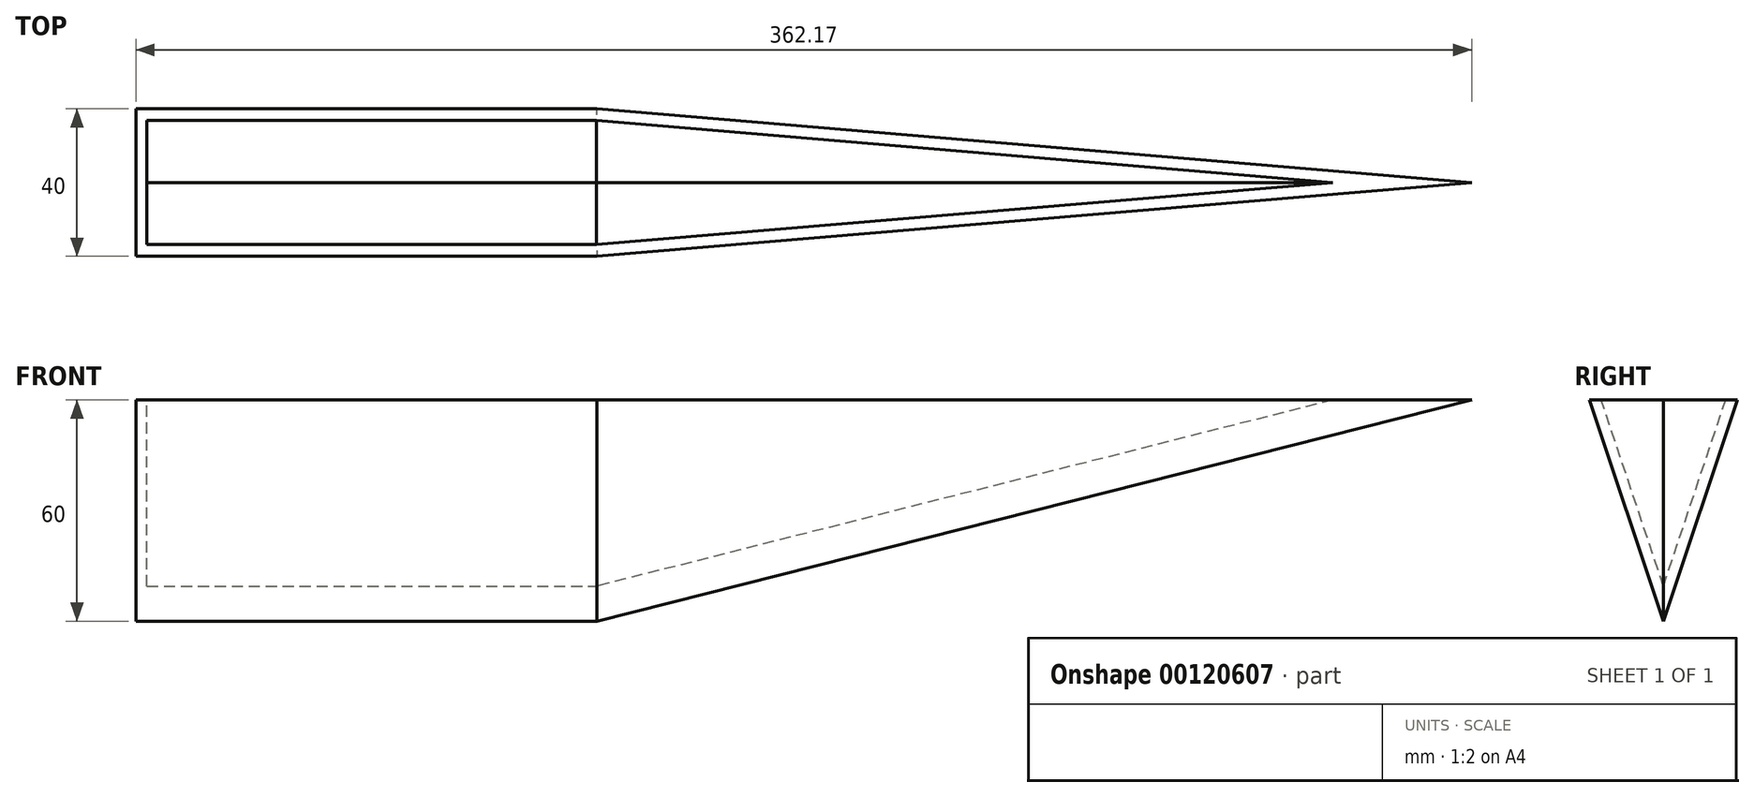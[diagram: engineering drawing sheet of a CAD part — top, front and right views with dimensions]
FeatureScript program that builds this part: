
annotation { "Feature Type Name" : "Feature", "Feature Type Description" : "" }
export const myFeature = defineFeature(function(context is Context, id is Id, definition is map)
    precondition{}
    {
        {
            var Q0;
            Q0=qCreatedBy(makeId("Front.planeOp"),FACE);
            var sketch = newSketch(context, id + "F0", { "sketchPlane" : qUnion([Q0])});
            skLineSegment(sketch, "E0.bottom", {"start": v(-391.71, 45.8) * mm, "end": v(-16.71, 45.8) * mm});
            skLineSegment(sketch, "E0.top", {"start": v(-391.71, -14.2) * mm, "end": v(-16.71, -14.2) * mm});
            skLineSegment(sketch, "E0.left", {"start": v(-391.71, 45.8) * mm, "end": v(-391.71, -14.2) * mm});
            skLineSegment(sketch, "E0.right", {"start": v(-16.71, 45.8) * mm, "end": v(-16.71, -14.2) * mm});
            skPoint(sketch, "E1.endSnap0", {"position": v(-204.21, -14.2) * mm});
            skSolve(sketch);
        }
        {
            var Q0;
            Q0=makeQuery(id+"F0.imprint","IMPRINT",FACE,{"disambiguationData":[TD([[makeQuery(id+"F0.imprint","IMPRINT",EDGE,{"derivedFrom":sQuery(id+"F0.wireOp",EDGE,"E0.bottom")}),-1.0]])]});
            extrude(context, id + "F1", {"entities" : qUnion([Q0]), "depth" : 40 * mm});
        }
        {
            var Q0;
            Q0=makeQuery(id+"F1.opExtrude","SWEPT_FACE",FACE,{"disambiguationData":[OSD([sQuery(id+"F0.wireOp",EDGE,"E0.left")])]});
            var sketch = newSketch(context, id + "F2", { "sketchPlane" : qUnion([Q0])});
            skLineSegment(sketch, "E2", {"start": v(20, -14.2) * mm, "end": v(0, 45.8) * mm});
            skLineSegment(sketch, "E3", {"start": v(20, -14.2) * mm, "end": v(40, 45.8) * mm});
            skSolve(sketch);
        }
        {
            var Q0;
            {var subQ0=sQuery(id+"F2.wireOp",EDGE,"E3");Q0=makeQuery(id+"F2.imprint","IMPRINT",FACE,{"disambiguationData":[TD([[makeQuery(id+"F2.imprint","IMPRINT",EDGE,{"derivedFrom":subQ0}),-1.0]])]});}
            extrude(context, id + "F3", {"entities" : qUnion([Q0]), "operationType" : NewBodyOperationType.ADD, "oppositeDirection" : true, "depth" : 375 * mm});
        }
        {
            var Q0;
            Q0=makeQuery(id+"F1.opExtrude","CAP_EDGE",EDGE,{"disambiguationData":[OSD([sQuery(id+"F0.wireOp",EDGE,"E0.top")])],"isStart":false});
            chamfer(context, id + "F4", {"entities" : qUnion([Q0]), "chamferType" : ChamferType.TWO_OFFSETS, "width1" : 60 * mm, "oppositeDirection" : false, "width2" : 20 * mm, "tangentPropagation" : true});
        }
        {
            var Q0;
            Q0=makeQuery(id+"F1.opExtrude","CAP_EDGE",EDGE,{"disambiguationData":[OSD([sQuery(id+"F0.wireOp",EDGE,"E0.top")])],"isStart":true});
            chamfer(context, id + "F5", {"entities" : qUnion([Q0]), "chamferType" : ChamferType.TWO_OFFSETS, "width1" : 20 * mm, "oppositeDirection" : false, "width2" : 60 * mm, "tangentPropagation" : true});
        }
        {
            var Q0;
            Q0=makeQuery(id+"F4.opChamfer","BLEND_EDGE",EDGE,{"blendedFrom":[makeQuery(id+"F1.opExtrude","CAP_EDGE",EDGE,{"disambiguationData":[OSD([sQuery(id+"F0.wireOp",EDGE,"E0.top")])],"isStart":false}),makeQuery(id+"F1.opExtrude","SWEPT_FACE",FACE,{"disambiguationData":[OSD([sQuery(id+"F0.wireOp",EDGE,"E0.right")])]})],"blendedInto":[makeQuery(id+"F1.opExtrude","SWEPT_FACE",FACE,{"disambiguationData":[OSD([sQuery(id+"F0.wireOp",EDGE,"E0.right")])]})]});
            chamfer(context, id + "F6", {"entities" : qUnion([Q0]), "chamferType" : ChamferType.TWO_OFFSETS, "width1" : 20 * mm, "oppositeDirection" : false, "width2" : 250 * mm, "tangentPropagation" : true});
        }
        {
            var Q0;
            Q0=makeQuery(id+"F5.opChamfer","BLEND_EDGE",EDGE,{"blendedFrom":[makeQuery(id+"F1.opExtrude","CAP_EDGE",EDGE,{"disambiguationData":[OSD([sQuery(id+"F0.wireOp",EDGE,"E0.top")])],"isStart":true}),makeQuery(id+"F1.opExtrude","SWEPT_FACE",FACE,{"disambiguationData":[OSD([sQuery(id+"F0.wireOp",EDGE,"E0.right")])]})],"blendedInto":[makeQuery(id+"F1.opExtrude","SWEPT_FACE",FACE,{"disambiguationData":[OSD([sQuery(id+"F0.wireOp",EDGE,"E0.right")])]})]});
            chamfer(context, id + "F7", {"entities" : qUnion([Q0]), "chamferType" : ChamferType.TWO_OFFSETS, "width1" : 20 * mm, "oppositeDirection" : false, "width2" : 250 * mm, "tangentPropagation" : true});
        }
        {
            var Q0;
            Q0=makeQuery(id+"F1.opExtrude","SWEPT_FACE",FACE,{"disambiguationData":[OSD([sQuery(id+"F0.wireOp",EDGE,"E0.bottom")])]});
            shell(context, id + "F8", {"entities" : qUnion([Q0]), "thickness" : 3 * mm});
        }
    });
